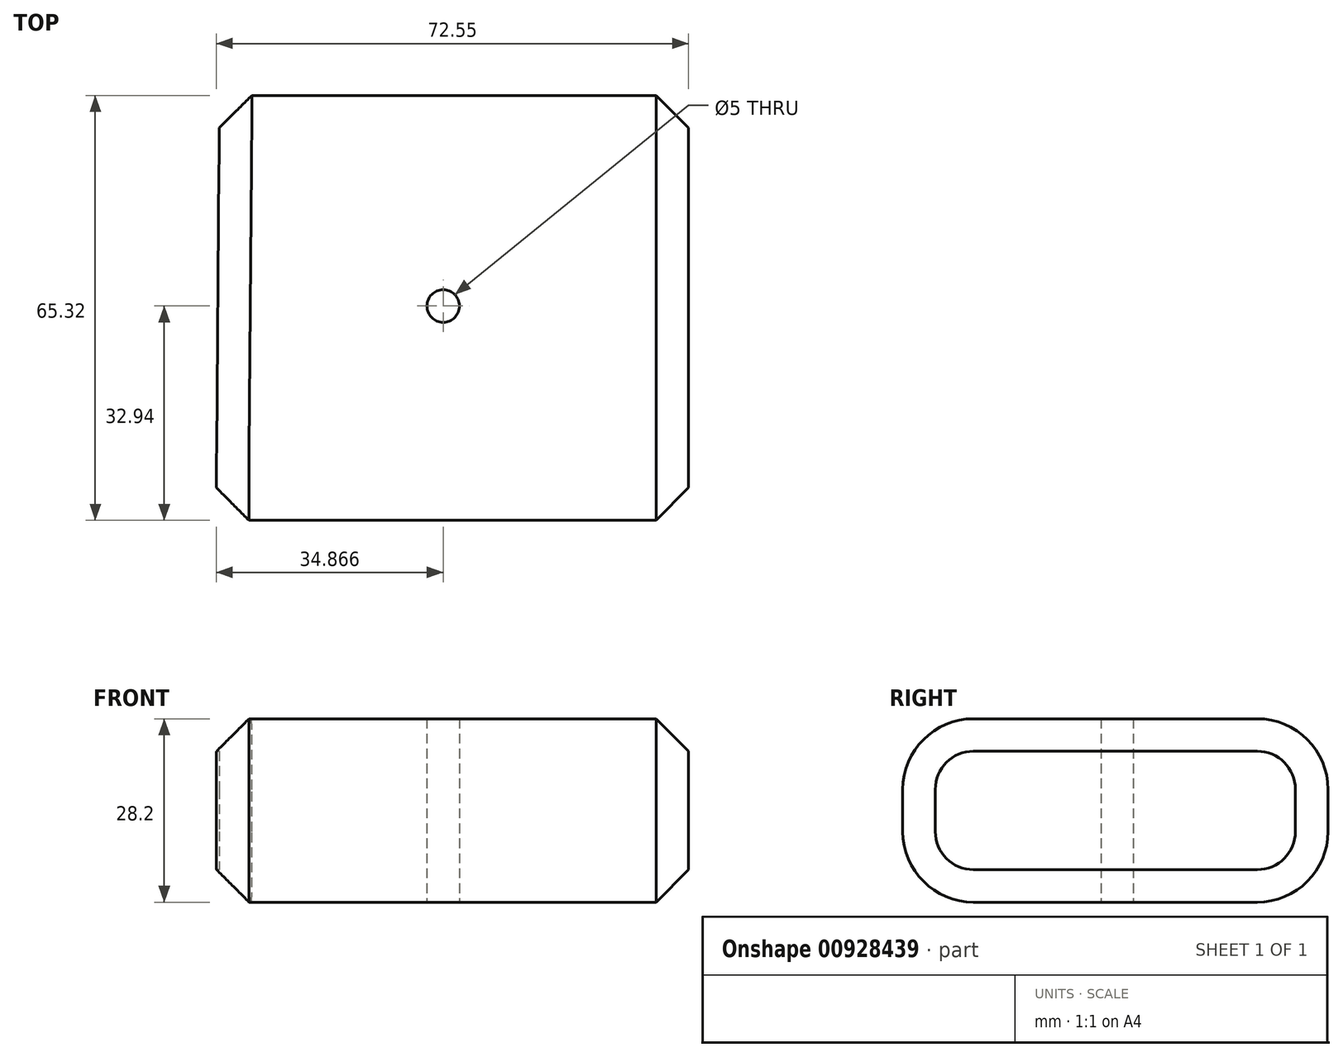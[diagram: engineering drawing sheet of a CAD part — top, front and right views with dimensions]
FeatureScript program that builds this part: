
annotation { "Feature Type Name" : "Feature", "Feature Type Description" : "" }
export const myFeature = defineFeature(function(context is Context, id is Id, definition is map)
    precondition{}
    {
        {
            var Q0;
            Q0=qCreatedBy(makeId("Top.planeOp"),FACE);
            var sketch = newSketch(context, id + "F0", { "sketchPlane" : qUnion([Q0])});
            skLineSegment(sketch, "E0", {"start": v(-42.36, 53.28) * mm, "end": v(29.67, 53.28) * mm});
            skLineSegment(sketch, "E1", {"start": v(29.67, 53.28) * mm, "end": v(29.67, -12.04) * mm});
            skLineSegment(sketch, "E2", {"start": v(29.67, -12.04) * mm, "end": v(-42.92, -12.04) * mm});
            skLineSegment(sketch, "E3", {"start": v(-42.92, -12.04) * mm, "end": v(-42.36, 53.28) * mm});
            skSolve(sketch);
        }
        {
            var Q0;
            Q0 = qSketchRegion(id + "F0", true);
            extrude(context, id + "F1", {"entities" : qUnion([Q0]), "depth" : 28.2 * mm, "offsetDistance" : 25 * mm});
        }
        {
            var Q0;
            Q0=makeQuery(id+"F1.opExtrude","CAP_EDGE",EDGE,{"disambiguationData":[OSD([sQuery(id+"F0.wireOp",EDGE,"E0")])],"isStart":false});
            var Q1;
            Q1=makeQuery(id+"F1.opExtrude","CAP_EDGE",EDGE,{"disambiguationData":[OSD([sQuery(id+"F0.wireOp",EDGE,"E0")])],"isStart":true});
            var Q2;
            Q2=makeQuery(id+"F1.opExtrude","CAP_EDGE",EDGE,{"disambiguationData":[OSD([sQuery(id+"F0.wireOp",EDGE,"E2")])],"isStart":true});
            var Q3;
            Q3=makeQuery(id+"F1.opExtrude","CAP_EDGE",EDGE,{"disambiguationData":[OSD([sQuery(id+"F0.wireOp",EDGE,"E2")])],"isStart":false});
            fillet(context, id + "F2", {"entities" : qUnion([Q0, Q1, Q2, Q3]), "radius" : 10.86 * mm, "tangentPropagation" : true, "allowEdgeOverflow" : false});
        }
        {
            var Q0;
            Q0=makeQuery(id+"F1.opExtrude","SWEPT_FACE",FACE,{"disambiguationData":[OSD([sQuery(id+"F0.wireOp",EDGE,"E3")])]});
            var Q1;
            Q1=makeQuery(id+"F1.opExtrude","SWEPT_FACE",FACE,{"disambiguationData":[OSD([sQuery(id+"F0.wireOp",EDGE,"E1")])]});
            chamfer(context, id + "F3", {"entities" : qUnion([Q0, Q1]), "width" : 5 * mm, "tangentPropagation" : true});
        }
        {
            var Q0;
            Q0=makeQuery(id+"F1.opExtrude","CAP_FACE",FACE,{"disambiguationData":[OSD([sQuery(id+"F0.wireOp",EDGE,"E0"),sQuery(id+"F0.wireOp",EDGE,"E1"),sQuery(id+"F0.wireOp",EDGE,"E2"),sQuery(id+"F0.wireOp",EDGE,"E3")])],"isStart":true});
            var sketch = newSketch(context, id + "F4", { "sketchPlane" : qUnion([Q0])});
            skCircle(sketch, "E4", {"center": v(-8.01, -20.9) * mm, "radius": 7.88 * mm});
            skSolve(sketch);
        }
        {
            var Q0;
            Q0=sQuery(id+"F4.wireOp",VERTEX,"E4.center");
            var Q1;
            Q1=makeQuery(id+"F1.opExtrude","SWEPT_BODY",BODY,{"disambiguationData":[OSD([sQuery(id+"F0.wireOp",EDGE,"E0"),sQuery(id+"F0.wireOp",EDGE,"E1"),sQuery(id+"F0.wireOp",EDGE,"E2"),sQuery(id+"F0.wireOp",EDGE,"E3")])]});
            hole(context, id + "F5", {"style" : HoleStyle.SIMPLE, "endStyle" : HoleEndStyle.THROUGH, "holeDiameter" : 5 * mm, "majorDiameter" : 5 * mm, "isTappedThrough" : true, "tappedDepth" : 12 * mm, "tapClearance" : 3, "locations" : qUnion([Q0]), "scope" : qUnion([Q1])});
        }
    });
